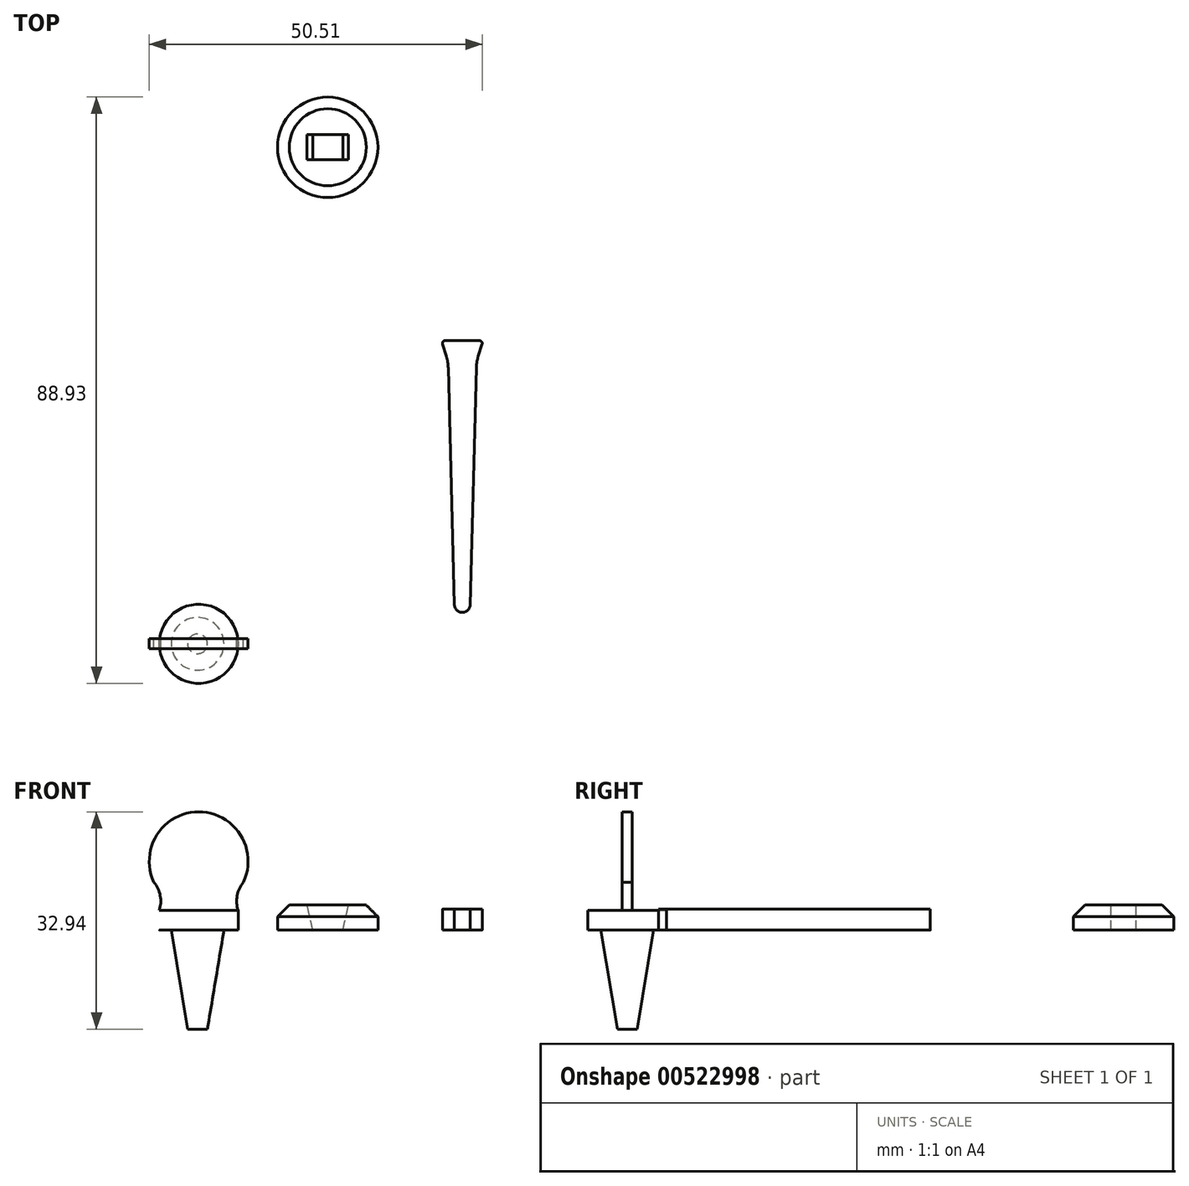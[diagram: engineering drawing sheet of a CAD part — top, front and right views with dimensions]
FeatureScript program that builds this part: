
annotation { "Feature Type Name" : "Feature", "Feature Type Description" : "" }
export const myFeature = defineFeature(function(context is Context, id is Id, definition is map)
    precondition{}
    {
        {
            var Q0;
            Q0=qCreatedBy(makeId("Top.planeOp"),FACE);
            var sketch = newSketch(context, id + "F0", { "sketchPlane" : qUnion([Q0])});
            skPoint(sketch, "E0.middle", {"position": v(0, 0) * mm});
            skLineSegment(sketch, "E1.bottom", {"start": v(7.91, 31.75) * mm, "end": v(5.64, 31.75) * mm});
            skLineSegment(sketch, "E1.top", {"start": v(2.47, 36.85) * mm, "end": v(-2.47, 36.85) * mm});
            skLineSegment(sketch, "E1.left", {"start": v(8.9, 31.75) * mm, "end": v(8.9, 33.37) * mm});
            skLineSegment(sketch, "E1.right", {"start": v(-8.9, 31.75) * mm, "end": v(-8.9, 33.37) * mm});
            skLineSegment(sketch, "E2.trimOffspring", {"start": v(-5.64, 31.75) * mm, "end": v(-7.91, 31.75) * mm});
            skLineSegment(sketch, "E3", {"start": v(-1.59, -22.87) * mm, "end": v(-3.1, 29.28) * mm});
            skLineSegment(sketch, "E4", {"start": v(3.1, 29.28) * mm, "end": v(1.59, -22.87) * mm});
            skPoint(sketch, "E5.visualSharp", {"position": v(-3.18, 31.75) * mm});
            skArc(sketch, "E5.filletArc", {"start": v(-3.1, 29.28) * mm, "mid": v(-3.87, 31.03) * mm, "end": v(-5.64, 31.75) * mm});
            skPoint(sketch, "E6.visualSharp", {"position": v(3.18, 31.75) * mm});
            skArc(sketch, "E6.filletArc", {"start": v(5.64, 31.75) * mm, "mid": v(3.87, 31.03) * mm, "end": v(3.1, 29.28) * mm});
            skLineSegment(sketch, "E7", {"start": v(-8.9, 33.37) * mm, "end": v(-8.85, 33.37) * mm});
            skArc(sketch, "E8", {"start": v(-4.36, 36.5) * mm, "mid": v(-6.68, 35.27) * mm, "end": v(-8.69, 33.58) * mm});
            skArc(sketch, "E9", {"start": v(8.69, 33.58) * mm, "mid": v(6.68, 35.27) * mm, "end": v(4.36, 36.5) * mm});
            skPoint(sketch, "E10.newPointA", {"position": v(-8.9, 31.75) * mm});
            skArc(sketch, "E10.filletArc", {"start": v(-8.69, 33.58) * mm, "mid": v(-8.9, 32.4) * mm, "end": v(-7.91, 31.75) * mm});
            skPoint(sketch, "E11.newPointA", {"position": v(8.9, 31.75) * mm});
            skArc(sketch, "E11.filletArc", {"start": v(7.91, 31.75) * mm, "mid": v(8.9, 32.4) * mm, "end": v(8.69, 33.58) * mm});
            skLineSegment(sketch, "E12.trimOffspring", {"start": v(8.85, 33.37) * mm, "end": v(8.9, 33.37) * mm});
            skPoint(sketch, "E13.visualSharp", {"position": v(-3.32, 36.85) * mm});
            skArc(sketch, "E13.filletArc", {"start": v(-2.47, 36.85) * mm, "mid": v(-3.44, 36.76) * mm, "end": v(-4.36, 36.5) * mm});
            skPoint(sketch, "E14.visualSharp", {"position": v(3.32, 36.85) * mm});
            skArc(sketch, "E14.filletArc", {"start": v(4.36, 36.5) * mm, "mid": v(3.44, 36.76) * mm, "end": v(2.47, 36.85) * mm});
            skArc(sketch, "E15", {"start": v(-1.59, -22.87) * mm, "mid": v(0, -24.41) * mm, "end": v(1.59, -22.87) * mm});
            skSolve(sketch);
        }
        {
            var Q0;
            Q0 = qSketchRegion(id + "F0", true);
            extrude(context, id + "F1", {"entities" : qUnion([Q0]), "depth" : 3.17 * mm, "offsetDistance" : 25.4 * mm});
        }
        {
            var Q0;
            Q0=qCreatedBy(makeId("Top.planeOp"),FACE);
            var sketch = newSketch(context, id + "F2", { "sketchPlane" : qUnion([Q0])});
            skPoint(sketch, "E16.middle", {"position": v(24.2, 0.24) * mm});
            skLineSegment(sketch, "E17.bottom", {"start": v(32.1, 31.99) * mm, "end": v(29.84, 31.99) * mm});
            skLineSegment(sketch, "E17.top", {"start": v(26.67, 37.1) * mm, "end": v(21.72, 37.1) * mm});
            skLineSegment(sketch, "E17.left", {"start": v(33.08, 31.99) * mm, "end": v(33.08, 33.61) * mm});
            skLineSegment(sketch, "E17.right", {"start": v(15.3, 31.99) * mm, "end": v(15.3, 33.61) * mm});
            skLineSegment(sketch, "E18.trimOffspring", {"start": v(29.84, 31.99) * mm, "end": v(28.86, 31.99) * mm});
            skLineSegment(sketch, "E19", {"start": v(15.3, 33.61) * mm, "end": v(15.34, 33.61) * mm});
            skArc(sketch, "E20", {"start": v(19.83, 36.73) * mm, "mid": v(17.51, 35.5) * mm, "end": v(15.5, 33.82) * mm});
            skArc(sketch, "E21", {"start": v(32.88, 33.82) * mm, "mid": v(30.87, 35.5) * mm, "end": v(28.56, 36.73) * mm});
            skPoint(sketch, "E22.newPointA", {"position": v(15.3, 31.99) * mm});
            skArc(sketch, "E22.filletArc", {"start": v(15.5, 33.82) * mm, "mid": v(15.29, 32.65) * mm, "end": v(16.28, 31.99) * mm});
            skArc(sketch, "E23.filletArc", {"start": v(32.1, 31.99) * mm, "mid": v(33.1, 32.65) * mm, "end": v(32.88, 33.82) * mm});
            skLineSegment(sketch, "E24.trimOffspring", {"start": v(33.04, 33.61) * mm, "end": v(33.08, 33.61) * mm});
            skPoint(sketch, "E25.visualSharp", {"position": v(20.87, 37.1) * mm});
            skArc(sketch, "E25.filletArc", {"start": v(21.72, 37.1) * mm, "mid": v(20.76, 37) * mm, "end": v(19.83, 36.73) * mm});
            skPoint(sketch, "E26.visualSharp", {"position": v(27.52, 37.1) * mm});
            skArc(sketch, "E26.filletArc", {"start": v(28.56, 36.73) * mm, "mid": v(27.63, 37) * mm, "end": v(26.67, 37.1) * mm});
            skLineSegment(sketch, "E27", {"start": v(23, -6.11) * mm, "end": v(22.06, 29.52) * mm});
            skLineSegment(sketch, "E28", {"start": v(25.39, -6.11) * mm, "end": v(26.32, 29.52) * mm});
            skPoint(sketch, "E29.orphan", {"position": v(22.03, 30.58) * mm});
            skPoint(sketch, "E30.orphan", {"position": v(26.35, 30.58) * mm});
            skLineSegment(sketch, "E31.trimOffspring", {"start": v(19.52, 31.99) * mm, "end": v(16.28, 31.99) * mm});
            skPoint(sketch, "E32.visualSharp", {"position": v(22, 31.99) * mm});
            skArc(sketch, "E32.filletArc", {"start": v(22.06, 29.52) * mm, "mid": v(21.3, 31.27) * mm, "end": v(19.52, 31.99) * mm});
            skPoint(sketch, "E33.visualSharp", {"position": v(26.39, 31.99) * mm});
            skArc(sketch, "E33.filletArc", {"start": v(28.86, 31.99) * mm, "mid": v(27.1, 31.27) * mm, "end": v(26.32, 29.52) * mm});
            skArc(sketch, "E34", {"start": v(23, -6.11) * mm, "mid": v(24.2, -7.27) * mm, "end": v(25.39, -6.11) * mm});
            skSolve(sketch);
        }
        {
            var Q0;
            Q0 = qSketchRegion(id + "F2", true);
            extrude(context, id + "F3", {"entities" : qUnion([Q0]), "depth" : 3.17 * mm, "offsetDistance" : 25.4 * mm});
        }
        {
            var Q0;
            Q0=makeQuery(id+"F1.opExtrude","SWEPT_BODY",BODY,{"disambiguationData":[OSD([sQuery(id+"F0.wireOp",EDGE,"E1.bottom"),sQuery(id+"F0.wireOp",EDGE,"E1.top"),sQuery(id+"F0.wireOp",EDGE,"E1.left"),sQuery(id+"F0.wireOp",EDGE,"E1.right"),sQuery(id+"F0.wireOp",EDGE,"E2.trimOffspring"),sQuery(id+"F0.wireOp",EDGE,"E3"),sQuery(id+"F0.wireOp",EDGE,"E4"),sQuery(id+"F0.wireOp",EDGE,"E5.filletArc"),sQuery(id+"F0.wireOp",EDGE,"E6.filletArc"),sQuery(id+"F0.wireOp",EDGE,"E7"),sQuery(id+"F0.wireOp",EDGE,"E8"),sQuery(id+"F0.wireOp",EDGE,"E9"),sQuery(id+"F0.wireOp",EDGE,"E10.filletArc"),sQuery(id+"F0.wireOp",EDGE,"E11.filletArc"),sQuery(id+"F0.wireOp",EDGE,"E12.trimOffspring"),sQuery(id+"F0.wireOp",EDGE,"E13.filletArc"),sQuery(id+"F0.wireOp",EDGE,"E14.filletArc"),sQuery(id+"F0.wireOp",EDGE,"E15")])]});
            deleteBodies(context, id + "F4", {"entities" : qUnion([Q0])});
        }
        {
            var Q0;
            Q0=qCreatedBy(makeId("Top.planeOp"),FACE);
            var sketch = newSketch(context, id + "F5", { "sketchPlane" : qUnion([Q0])});
            skLineSegment(sketch, "E35.top", {"start": v(1.23, -17.78) * mm, "end": v(1.2, -17.78) * mm});
            skPoint(sketch, "E35.middle", {"position": v(0, 0) * mm});
            skLineSegment(sketch, "E36.top", {"start": v(1.2, -19.05) * mm, "end": v(-1.2, -19.05) * mm});
            skLineSegment(sketch, "E36.left", {"start": v(1.2, -17.78) * mm, "end": v(1.2, -19.05) * mm});
            skLineSegment(sketch, "E36.right", {"start": v(-1.2, -17.78) * mm, "end": v(-1.2, -19.05) * mm});
            skLineSegment(sketch, "E37", {"start": v(-1.2, -19.05) * mm, "end": v(-2.14, 16.88) * mm});
            skLineSegment(sketch, "E38", {"start": v(1.2, -19.05) * mm, "end": v(2.14, 16.88) * mm});
            skPoint(sketch, "E39.orphan", {"position": v(-2.16, -17.78) * mm});
            skLineSegment(sketch, "E40.trimOffspring", {"start": v(-1.2, -17.78) * mm, "end": v(-1.23, -17.78) * mm});
            skPoint(sketch, "E35.left.end.orphan", {"position": v(2.16, -17.78) * mm});
            skLineSegment(sketch, "E41.top", {"start": v(-2.6, 20.98) * mm, "end": v(2.6, 20.98) * mm});
            skLineSegment(sketch, "E42", {"start": v(-2.43, 18.64) * mm, "end": v(-3, 20.43) * mm});
            skPoint(sketch, "E43.orphan", {"position": v(-3.18, 17.78) * mm});
            skPoint(sketch, "E44.orphan", {"position": v(1.2, 19.05) * mm});
            skPoint(sketch, "E45.orphan", {"position": v(-1.2, 19.05) * mm});
            skLineSegment(sketch, "E46", {"start": v(2.43, 18.64) * mm, "end": v(3, 20.43) * mm});
            skArc(sketch, "E47", {"start": v(-1.2, -19.05) * mm, "mid": v(0, -20.24) * mm, "end": v(1.2, -19.05) * mm});
            skPoint(sketch, "E48.visualSharp", {"position": v(-2.16, 17.78) * mm});
            skArc(sketch, "E48.filletArc", {"start": v(-2.14, 16.88) * mm, "mid": v(-2.22, 17.77) * mm, "end": v(-2.43, 18.64) * mm});
            skPoint(sketch, "E49.visualSharp", {"position": v(2.16, 17.78) * mm});
            skArc(sketch, "E49.filletArc", {"start": v(2.43, 18.64) * mm, "mid": v(2.22, 17.77) * mm, "end": v(2.14, 16.88) * mm});
            skPoint(sketch, "E50.visualSharp", {"position": v(3.17, 20.98) * mm});
            skArc(sketch, "E50.filletArc", {"start": v(3, 20.43) * mm, "mid": v(2.94, 20.81) * mm, "end": v(2.6, 20.98) * mm});
            skPoint(sketch, "E51.visualSharp", {"position": v(-3.18, 20.98) * mm});
            skArc(sketch, "E51.filletArc", {"start": v(-2.6, 20.98) * mm, "mid": v(-2.94, 20.81) * mm, "end": v(-3, 20.43) * mm});
            skSolve(sketch);
        }
        {
            var Q0;
            Q0 = qSketchRegion(id + "F5", true);
            extrude(context, id + "F6", {"entities" : qUnion([Q0]), "depth" : 3.17 * mm, "offsetDistance" : 25.4 * mm});
        }
        {
            var Q0;
            Q0=qCreatedBy(makeId("Top.planeOp"),FACE);
            var sketch = newSketch(context, id + "F7", { "sketchPlane" : qUnion([Q0])});
            skCircle(sketch, "E52", {"center": v(-20.4, 50.3) * mm, "radius": 7.62 * mm});
            skLineSegment(sketch, "E53", {"start": v(-10.32, 50.3) * mm, "end": v(-30.77, 50.3) * mm, "construction": true});
            skSolve(sketch);
        }
        {
            var Q0;
            Q0 = qSketchRegion(id + "F7", true);
            extrude(context, id + "F8", {"entities" : qUnion([Q0]), "depth" : 3.8 * mm, "offsetDistance" : 25.4 * mm});
        }
        {
            var Q0;
            Q0=sQuery(id+"F7.wireOp",EDGE,"E53");
            cPlane(context, id + "F9", {"entities" : qUnion([Q0]), "cplaneType" : CPlaneType.LINE_ANGLE, "offset" : 25.4 * mm, "angle" : 0 * degree, "width" : 152.4 * mm, "height" : 152.4 * mm});
        }
        {
            var Q0;
            Q0=qCreatedBy(id+"F9.planeOp",FACE);
            var sketch = newSketch(context, id + "F10", { "sketchPlane" : qUnion([Q0])});
            skLineSegment(sketch, "E54.bottom", {"start": v(-23.58, 3.96) * mm, "end": v(-17.23, 3.96) * mm});
            skPoint(sketch, "E54.middle", {"position": v(-20.4, 0) * mm});
            skPoint(sketch, "E55.top.start.orphan", {"position": v(-22.57, 3.36) * mm});
            skPoint(sketch, "E55.right.end.orphan", {"position": v(-18.25, 3.36) * mm});
            skPoint(sketch, "E54.top.end.orphan", {"position": v(-17.23, -3.96) * mm});
            skPoint(sketch, "E54.left.end.orphan", {"position": v(-23.58, -3.96) * mm});
            skLineSegment(sketch, "E56.bottom", {"start": v(-18.25, -0.58) * mm, "end": v(-22.57, -0.58) * mm});
            skLineSegment(sketch, "E57", {"start": v(-22.57, -0.58) * mm, "end": v(-23.58, 3.96) * mm});
            skLineSegment(sketch, "E58", {"start": v(-18.25, -0.58) * mm, "end": v(-17.23, 3.96) * mm});
            skPoint(sketch, "E56.right.end.orphan", {"position": v(-22.57, 0.58) * mm});
            skPoint(sketch, "E56.left.end.orphan", {"position": v(-18.25, 0.58) * mm});
            skPoint(sketch, "E55.bottom.end.orphan", {"position": v(-18.25, -3.36) * mm});
            skPoint(sketch, "E55.bottom.start.orphan", {"position": v(-22.57, -3.36) * mm});
            skSolve(sketch);
        }
        {
            var Q0;
            Q0 = qSketchRegion(id + "F10", true);
            extrude(context, id + "F11", {"entities" : qUnion([Q0]), "operationType" : NewBodyOperationType.REMOVE, "oppositeDirection" : true, "depth" : 3.8 * mm, "offsetDistance" : 25.4 * mm, "symmetric" : true});
        }
        {
            var Q0;
            Q0=makeQuery(id+"F8.opExtrude","CAP_EDGE",EDGE,{"disambiguationData":[OSD([sQuery(id+"F7.wireOp",EDGE,"E52")])],"isStart":false});
            chamfer(context, id + "F12", {"entities" : qUnion([Q0]), "width" : 1.78 * mm, "tangentPropagation" : true});
        }
        {
            var Q0;
            Q0=makeQuery(id+"F3.opExtrude","SWEPT_BODY",BODY,{"disambiguationData":[OSD([sQuery(id+"F2.wireOp",EDGE,"E17.bottom"),sQuery(id+"F2.wireOp",EDGE,"E17.top"),sQuery(id+"F2.wireOp",EDGE,"E17.left"),sQuery(id+"F2.wireOp",EDGE,"E17.right"),sQuery(id+"F2.wireOp",EDGE,"E18.trimOffspring"),sQuery(id+"F2.wireOp",EDGE,"E19"),sQuery(id+"F2.wireOp",EDGE,"E20"),sQuery(id+"F2.wireOp",EDGE,"E21"),sQuery(id+"F2.wireOp",EDGE,"E22.filletArc"),sQuery(id+"F2.wireOp",EDGE,"E23.filletArc"),sQuery(id+"F2.wireOp",EDGE,"E24.trimOffspring"),sQuery(id+"F2.wireOp",EDGE,"E25.filletArc"),sQuery(id+"F2.wireOp",EDGE,"E26.filletArc"),sQuery(id+"F2.wireOp",EDGE,"E27"),sQuery(id+"F2.wireOp",EDGE,"E28"),sQuery(id+"F2.wireOp",EDGE,"E31.trimOffspring"),sQuery(id+"F2.wireOp",EDGE,"E32.filletArc"),sQuery(id+"F2.wireOp",EDGE,"E33.filletArc"),sQuery(id+"F2.wireOp",EDGE,"E34")])]});
            deleteBodies(context, id + "F13", {"entities" : qUnion([Q0])});
        }
        {
            var Q0;
            Q0=qCreatedBy(makeId("Front.planeOp"),FACE);
            cPlane(context, id + "F14", {"entities" : qUnion([Q0]), "cplaneType" : CPlaneType.OFFSET, "offset" : 25 * mm, "width" : 150 * mm, "height" : 150 * mm});
        }
        {
            var Q0;
            Q0=qCreatedBy(makeId("Top.planeOp"),FACE);
            var sketch = newSketch(context, id + "F15", { "sketchPlane" : qUnion([Q0])});
            skCircle(sketch, "E59", {"center": v(-40, -25) * mm, "radius": 6 * mm});
            skSolve(sketch);
        }
        {
            var Q0;
            Q0 = qSketchRegion(id + "F15", true);
            extrude(context, id + "F16", {"entities" : qUnion([Q0]), "depth" : 3 * mm, "offsetDistance" : 25 * mm});
        }
        {
            var Q0;
            Q0=makeQuery(id+"F16.opExtrude","CAP_FACE",FACE,{"disambiguationData":[OSD([sQuery(id+"F15.wireOp",EDGE,"E59")])],"isStart":false});
            var sketch = newSketch(context, id + "F17", { "sketchPlane" : qUnion([Q0])});
            skLineSegment(sketch, "E60", {"start": v(-46, -25) * mm, "end": v(-34, -25) * mm, "construction": true});
            skSolve(sketch);
        }
        {
            var Q0;
            Q0=qCreatedBy(id+"F14.planeOp",FACE);
            var sketch = newSketch(context, id + "F18", { "sketchPlane" : qUnion([Q0])});
            skLineSegment(sketch, "E61", {"start": v(-40, 2.94) * mm, "end": v(-40, 17.94) * mm, "construction": true});
            skLineSegment(sketch, "E62", {"start": v(-47.5, 10.44) * mm, "end": v(-32.5, 10.44) * mm, "construction": true});
            skPoint(sketch, "E62.startSnap0", {"position": v(-40, 10.44) * mm});
            skArc(sketch, "E63", {"start": v(-33.2, 7.27) * mm, "mid": v(-40, 17.94) * mm, "end": v(-46.79, 7.27) * mm});
            skLineSegment(sketch, "E64", {"start": v(-45.98, 3) * mm, "end": v(-34, 3) * mm});
            skArc(sketch, "E65", {"start": v(-45.98, 3) * mm, "mid": v(-45.83, 5.24) * mm, "end": v(-46.79, 7.27) * mm});
            skPoint(sketch, "E65.third.point", {"position": v(-50.9, 0) * mm});
            skArc(sketch, "E66", {"start": v(-33.2, 7.27) * mm, "mid": v(-34.16, 5.24) * mm, "end": v(-34, 3) * mm});
            skPoint(sketch, "E66.third.point", {"position": v(-29.4, 0) * mm});
            skSolve(sketch);
        }
        {
            var Q0;
            Q0 = qSketchRegion(id + "F18", true);
            extrude(context, id + "F19", {"entities" : qUnion([Q0]), "operationType" : NewBodyOperationType.ADD, "depth" : 1.5 * mm, "offsetDistance" : 25 * mm, "symmetric" : true});
        }
        {
            var Q0;
            Q0=qCreatedBy(id+"F14.planeOp",FACE);
            var sketch = newSketch(context, id + "F20", { "sketchPlane" : qUnion([Q0])});
            skLineSegment(sketch, "E67", {"start": v(-40.17, 0) * mm, "end": v(-40.17, -15) * mm});
            skLineSegment(sketch, "E68", {"start": v(-40.17, -15) * mm, "end": v(-41.67, -15) * mm});
            skLineSegment(sketch, "E69", {"start": v(-41.67, -15) * mm, "end": v(-44.17, 0) * mm});
            skLineSegment(sketch, "E70", {"start": v(-44.17, 0) * mm, "end": v(-40.17, 0) * mm});
            skSolve(sketch);
        }
        {
            var Q0;
            Q0=makeQuery(id+"F20.imprint","IMPRINT",FACE,{"disambiguationData":[TD([[makeQuery(id+"F20.imprint","IMPRINT",EDGE,{"derivedFrom":sQuery(id+"F20.wireOp",EDGE,"E67")}),-1.0]])]});
            var Q1;
            Q1=sQuery(id+"F20.wireOp",EDGE,"E67");
            revolve(context, id + "F21", {"operationType" : NewBodyOperationType.ADD, "surfaceOperationType" : NewSurfaceOperationType.NEW, "entities" : qUnion([Q0]), "axis" : qUnion([Q1]), "revolveType" : RevolveType.FULL});
        }
    });
